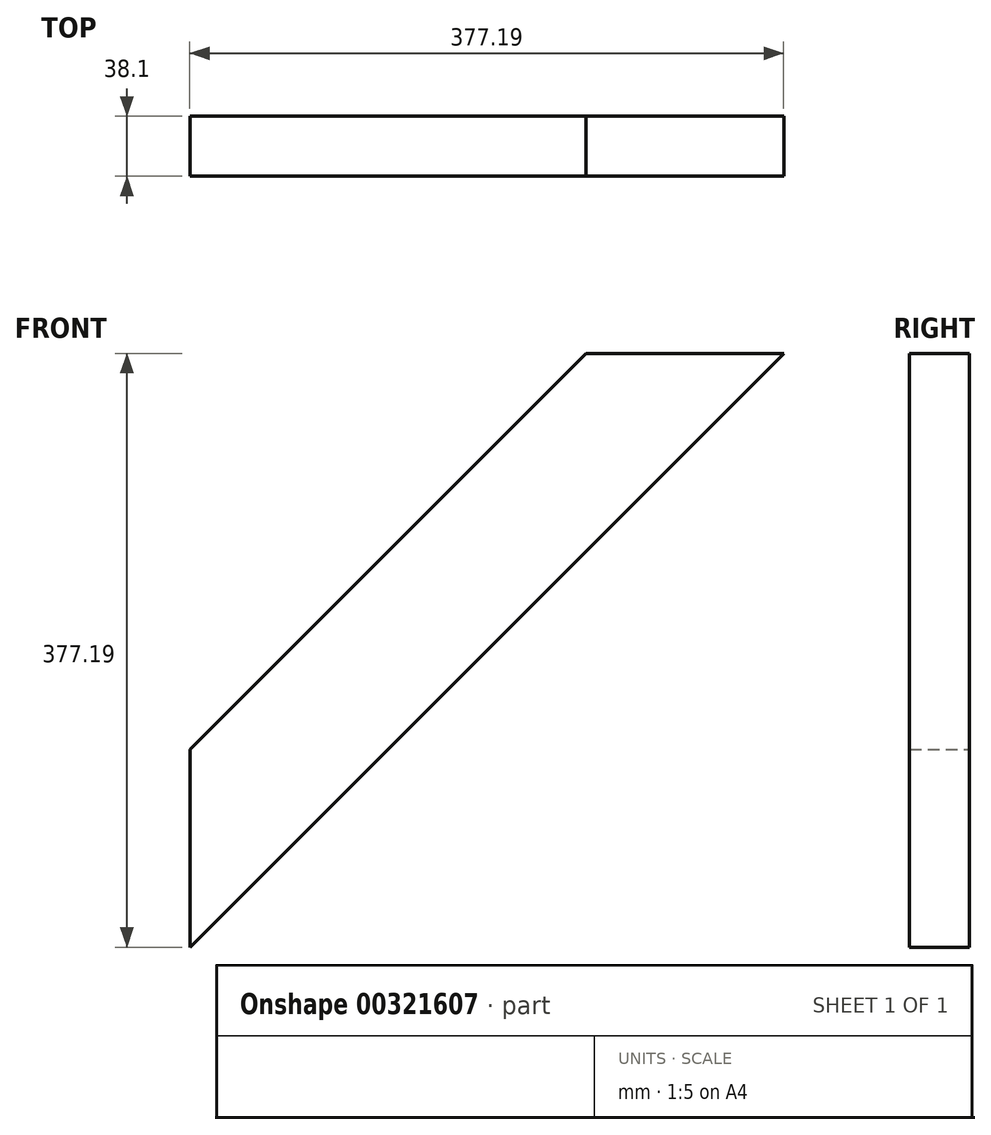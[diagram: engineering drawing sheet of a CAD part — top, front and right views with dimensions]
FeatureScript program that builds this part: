
annotation { "Feature Type Name" : "Feature", "Feature Type Description" : "" }
export const myFeature = defineFeature(function(context is Context, id is Id, definition is map)
    precondition{}
    {
        {
            var Q0;
            Q0=qCreatedBy(makeId("Front.planeOp"),FACE);
            var sketch = newSketch(context, id + "F0", { "sketchPlane" : qUnion([Q0])});
            skLineSegment(sketch, "E0", {"start": v(-155.34, 128.74) * mm, "end": v(-29.6, 128.74) * mm});
            skLineSegment(sketch, "E1", {"start": v(-29.6, 128.74) * mm, "end": v(-406.8, -248.45) * mm});
            skLineSegment(sketch, "E2", {"start": v(-406.8, -248.45) * mm, "end": v(-406.8, -122.72) * mm});
            skLineSegment(sketch, "E3", {"start": v(-406.8, -122.72) * mm, "end": v(-155.34, 128.74) * mm});
            skSolve(sketch);
        }
        {
            var Q0;
            Q0=makeQuery(id+"F0.imprint","IMPRINT",FACE,{"disambiguationData":[TD([[makeQuery(id+"F0.imprint","IMPRINT",EDGE,{"derivedFrom":sQuery(id+"F0.wireOp",EDGE,"E0")}),-1.0]])]});
            extrude(context, id + "F1", {"entities" : qUnion([Q0]), "depth" : 38.1 * mm});
        }
    });
